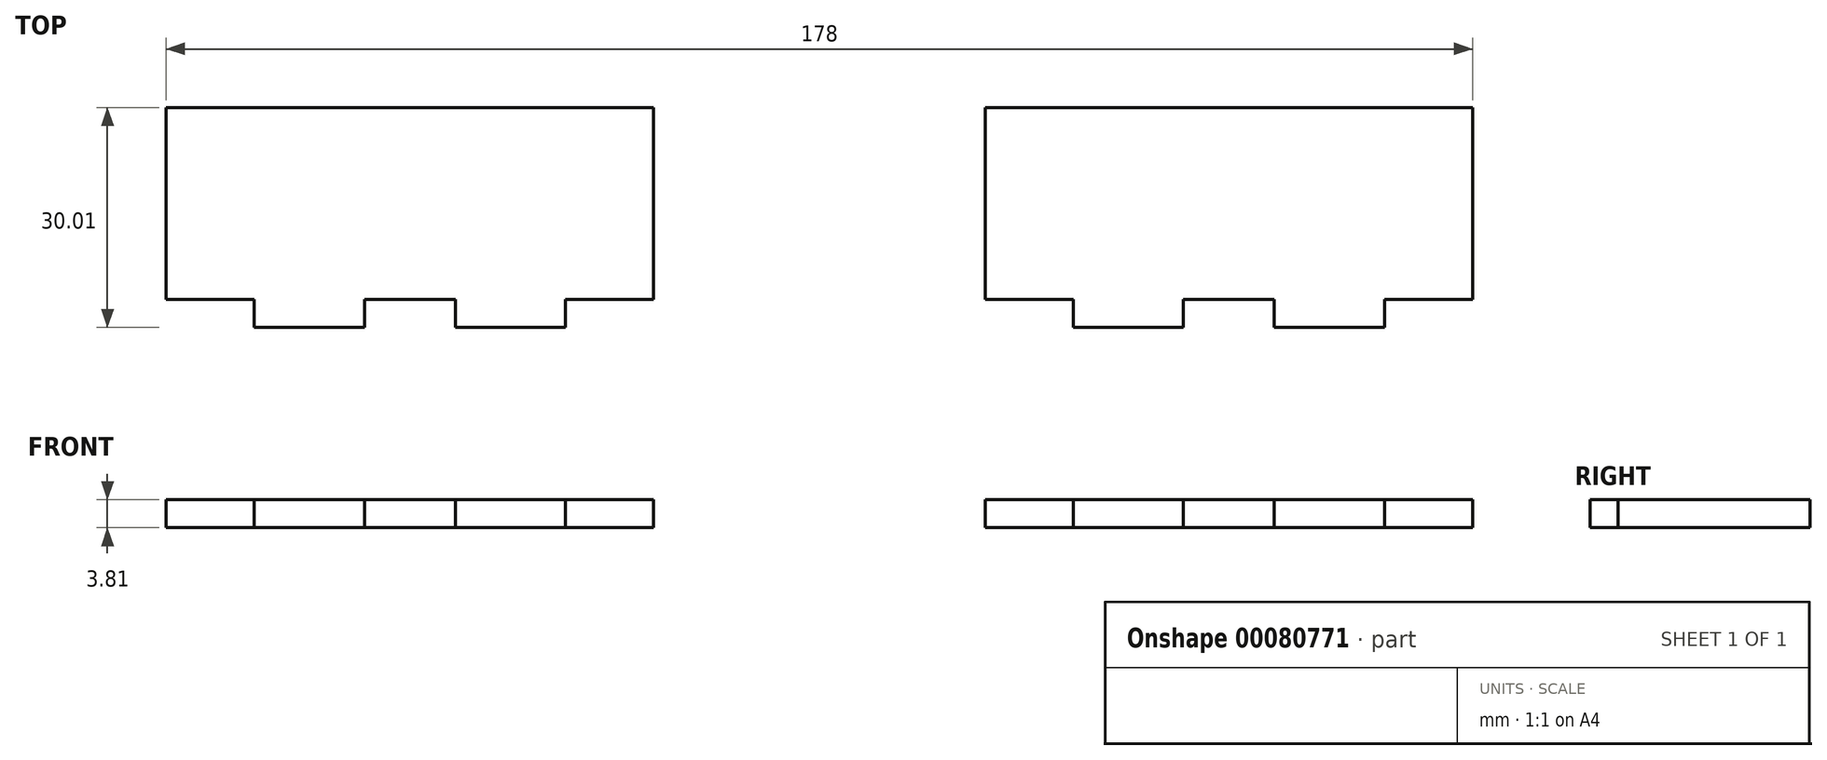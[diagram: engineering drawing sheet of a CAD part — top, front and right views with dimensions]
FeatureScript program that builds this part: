
annotation { "Feature Type Name" : "Feature", "Feature Type Description" : "" }
export const myFeature = defineFeature(function(context is Context, id is Id, definition is map)
    precondition{}
    {
        {
            var Q0;
            Q0=qCreatedBy(makeId("Top.planeOp"),FACE);
            var sketch = newSketch(context, id + "F0", { "sketchPlane" : qUnion([Q0])});
            skLineSegment(sketch, "E0.bottom", {"start": v(89, 13.1) * mm, "end": v(-89, 13.1) * mm});
            skLineSegment(sketch, "E0.top", {"start": v(89, -13.1) * mm, "end": v(-89, -13.1) * mm});
            skLineSegment(sketch, "E0.left", {"start": v(89, 13.1) * mm, "end": v(89, -13.1) * mm});
            skLineSegment(sketch, "E0.right", {"start": v(-89, 13.1) * mm, "end": v(-89, -13.1) * mm});
            skPoint(sketch, "E0.middle", {"position": v(0, 0) * mm});
            skLineSegment(sketch, "E1", {"start": v(-22.58, 13.1) * mm, "end": v(-22.58, -13.1) * mm});
            skLineSegment(sketch, "E2", {"start": v(0, 13.1) * mm, "end": v(0, -13.1) * mm});
            skLineSegment(sketch, "E3.MirrorCS", {"start": v(22.58, 13.1) * mm, "end": v(22.58, -13.1) * mm});
            skLineSegment(sketch, "E4", {"start": v(-77, -13.1) * mm, "end": v(-77, -16.9) * mm});
            skLineSegment(sketch, "E5", {"start": v(-77, -16.9) * mm, "end": v(-62, -16.9) * mm});
            skLineSegment(sketch, "E6", {"start": v(-62, -16.9) * mm, "end": v(-62, -13.1) * mm});
            skLineSegment(sketch, "E7", {"start": v(-49.58, -13.1) * mm, "end": v(-49.58, -16.9) * mm});
            skLineSegment(sketch, "E8", {"start": v(-49.58, -16.9) * mm, "end": v(-34.58, -16.9) * mm});
            skLineSegment(sketch, "E9", {"start": v(-34.58, -16.9) * mm, "end": v(-34.58, -13.1) * mm});
            skLineSegment(sketch, "E10.MirrorCS", {"start": v(34.58, -16.9) * mm, "end": v(34.58, -13.1) * mm});
            skLineSegment(sketch, "E11.MirrorCS", {"start": v(49.58, -16.9) * mm, "end": v(34.58, -16.9) * mm});
            skLineSegment(sketch, "E12.MirrorCS", {"start": v(49.58, -13.1) * mm, "end": v(49.58, -16.9) * mm});
            skLineSegment(sketch, "E13.MirrorCS", {"start": v(62, -16.9) * mm, "end": v(62, -13.1) * mm});
            skLineSegment(sketch, "E14.MirrorCS", {"start": v(77, -16.9) * mm, "end": v(62, -16.9) * mm});
            skLineSegment(sketch, "E15.MirrorCS", {"start": v(77, -13.1) * mm, "end": v(77, -16.9) * mm});
            skSolve(sketch);
        }
        {
            var Q0;
            {var subQ3=sQuery(id+"F0.wireOp",EDGE,"E0.right");Q0=makeQuery(id+"F0.imprint","IMPRINT",FACE,{"disambiguationData":[TD([[makeQuery(id+"F0.imprint","IMPRINT",EDGE,{"derivedFrom":subQ3}),1.0]])]});}
            var Q1;
            {var subQ0=sQuery(id+"F0.wireOp",EDGE,"E4");Q1=makeQuery(id+"F0.imprint","IMPRINT",FACE,{"disambiguationData":[TD([[makeQuery(id+"F0.imprint","IMPRINT",EDGE,{"derivedFrom":subQ0}),1.0]])]});}
            var Q2;
            {var subQ0=sQuery(id+"F0.wireOp",EDGE,"E7");Q2=makeQuery(id+"F0.imprint","IMPRINT",FACE,{"disambiguationData":[TD([[makeQuery(id+"F0.imprint","IMPRINT",EDGE,{"derivedFrom":subQ0}),1.0]])]});}
            var Q3;
            {var subQ4=sQuery(id+"F0.wireOp",EDGE,"E0.left");Q3=makeQuery(id+"F0.imprint","IMPRINT",FACE,{"disambiguationData":[TD([[makeQuery(id+"F0.imprint","IMPRINT",EDGE,{"derivedFrom":subQ4}),-1.0]])]});}
            var Q4;
            {var subQ0=sQuery(id+"F0.wireOp",EDGE,"E10.MirrorCS");Q4=makeQuery(id+"F0.imprint","IMPRINT",FACE,{"disambiguationData":[TD([[makeQuery(id+"F0.imprint","IMPRINT",EDGE,{"derivedFrom":subQ0}),-1.0]])]});}
            var Q5;
            {var subQ0=sQuery(id+"F0.wireOp",EDGE,"E13.MirrorCS");Q5=makeQuery(id+"F0.imprint","IMPRINT",FACE,{"disambiguationData":[TD([[makeQuery(id+"F0.imprint","IMPRINT",EDGE,{"derivedFrom":subQ0}),-1.0]])]});}
            extrude(context, id + "F1", {"entities" : qUnion([Q0, Q1, Q2, Q3, Q4, Q5]), "depth" : 3.8 * mm});
        }
    });
